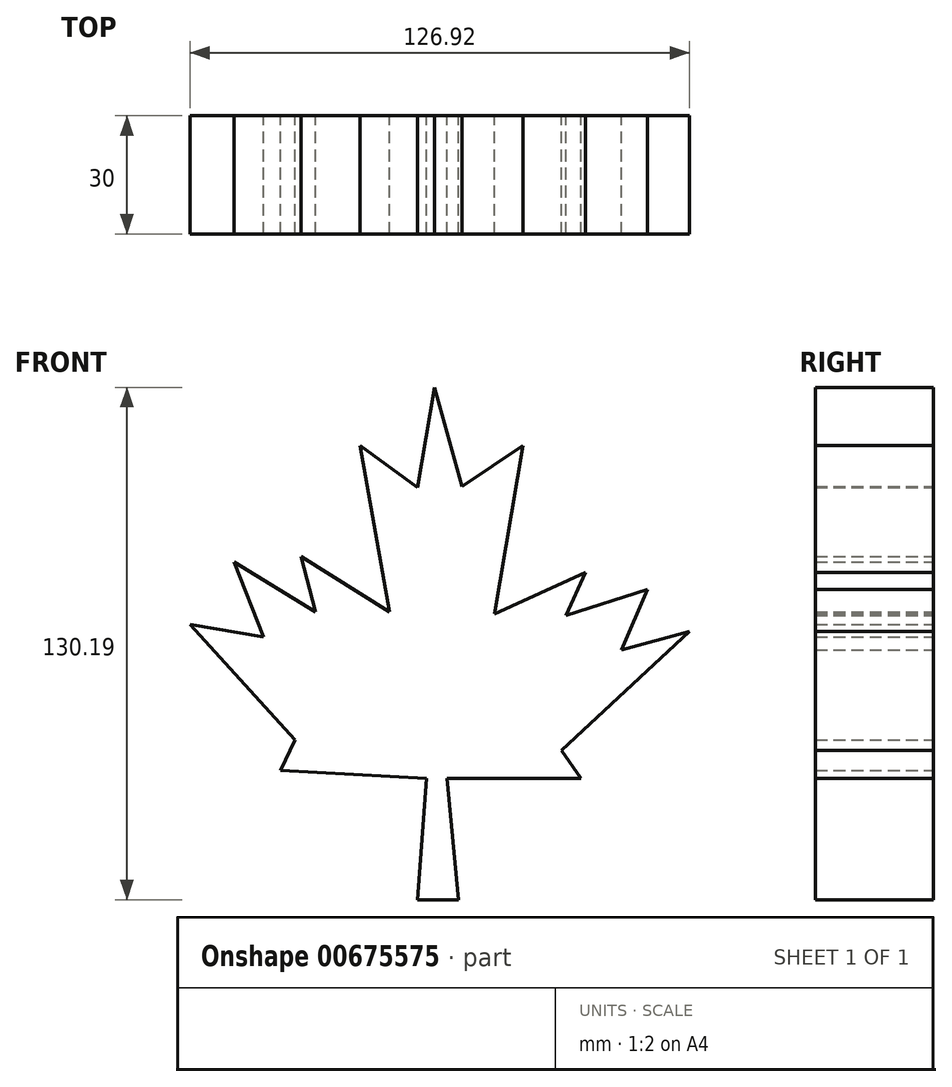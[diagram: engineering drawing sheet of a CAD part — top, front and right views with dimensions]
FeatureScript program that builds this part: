
annotation { "Feature Type Name" : "Feature", "Feature Type Description" : "" }
export const myFeature = defineFeature(function(context is Context, id is Id, definition is map)
    precondition{}
    {
        {
            var Q0;
            Q0=qCreatedBy(makeId("Front.planeOp"),FACE);
            var sketch = newSketch(context, id + "F0", { "sketchPlane" : qUnion([Q0])});
            skLineSegment(sketch, "E0", {"start": v(-39.57, -30.65) * mm, "end": v(-35.83, -22.88) * mm});
            skLineSegment(sketch, "E1", {"start": v(-30.65, 9.64) * mm, "end": v(-34.4, 23.74) * mm});
            skLineSegment(sketch, "E2", {"start": v(-34.4, 23.74) * mm, "end": v(-11.94, 9.64) * mm});
            skLineSegment(sketch, "E3", {"start": v(-11.94, 9.64) * mm, "end": v(-19.43, 51.95) * mm});
            skLineSegment(sketch, "E4", {"start": v(-30.65, 9.64) * mm, "end": v(-51.37, 22.3) * mm});
            skLineSegment(sketch, "E5", {"start": v(-51.37, 22.3) * mm, "end": v(-43.9, 3.3) * mm});
            skLineSegment(sketch, "E6", {"start": v(-43.9, 3.3) * mm, "end": v(-62.6, 6.48) * mm});
            skPoint(sketch, "E7.end.orphan", {"position": v(-59.14, 0) * mm});
            skLineSegment(sketch, "E8", {"start": v(-35.83, -22.88) * mm, "end": v(-62.6, 6.48) * mm});
            skLineSegment(sketch, "E9", {"start": v(-19.43, 51.95) * mm, "end": v(-4.75, 41.3) * mm});
            skLineSegment(sketch, "E10", {"start": v(-4.75, 41.3) * mm, "end": v(-0.45, 66.73) * mm});
            skLineSegment(sketch, "E11", {"start": v(-0.45, 66.73) * mm, "end": v(6.48, 41.59) * mm});
            skLineSegment(sketch, "E12", {"start": v(6.48, 41.59) * mm, "end": v(22.02, 51.95) * mm});
            skLineSegment(sketch, "E13", {"start": v(22.02, 51.95) * mm, "end": v(14.78, 9.17) * mm});
            skLineSegment(sketch, "E14", {"start": v(14.78, 9.17) * mm, "end": v(37.85, 19.71) * mm});
            skLineSegment(sketch, "E15", {"start": v(37.85, 19.71) * mm, "end": v(32.95, 8.78) * mm});
            skLineSegment(sketch, "E16", {"start": v(32.95, 8.78) * mm, "end": v(53.68, 15.4) * mm});
            skPoint(sketch, "E17.end.orphan", {"position": v(40.44, 0) * mm});
            skPoint(sketch, "E18.start.orphan", {"position": v(-11.94, -26.33) * mm});
            skLineSegment(sketch, "E19", {"start": v(-4.75, -63.46) * mm, "end": v(5.61, -63.46) * mm});
            skLineSegment(sketch, "E20", {"start": v(-4.75, -63.46) * mm, "end": v(-2.45, -32.67) * mm});
            skLineSegment(sketch, "E21", {"start": v(-2.45, -32.67) * mm, "end": v(-39.57, -30.65) * mm});
            skLineSegment(sketch, "E22", {"start": v(5.61, -63.46) * mm, "end": v(2.73, -32.67) * mm});
            skLineSegment(sketch, "E23", {"start": v(2.73, -32.67) * mm, "end": v(36.7, -32.67) * mm});
            skLineSegment(sketch, "E24", {"start": v(36.7, -32.67) * mm, "end": v(31.8, -25.47) * mm});
            skLineSegment(sketch, "E25", {"start": v(31.8, -25.47) * mm, "end": v(64.32, 4.75) * mm});
            skLineSegment(sketch, "E26", {"start": v(64.32, 4.75) * mm, "end": v(47.06, 0) * mm});
            skLineSegment(sketch, "E27", {"start": v(47.06, 0) * mm, "end": v(53.68, 15.4) * mm});
            skSolve(sketch);
        }
        {
            var Q0;
            Q0 = qSketchRegion(id + "F0", true);
            extrude(context, id + "F1", {"entities" : qUnion([Q0]), "depth" : 30 * mm, "offsetDistance" : 25 * mm});
        }
    });
